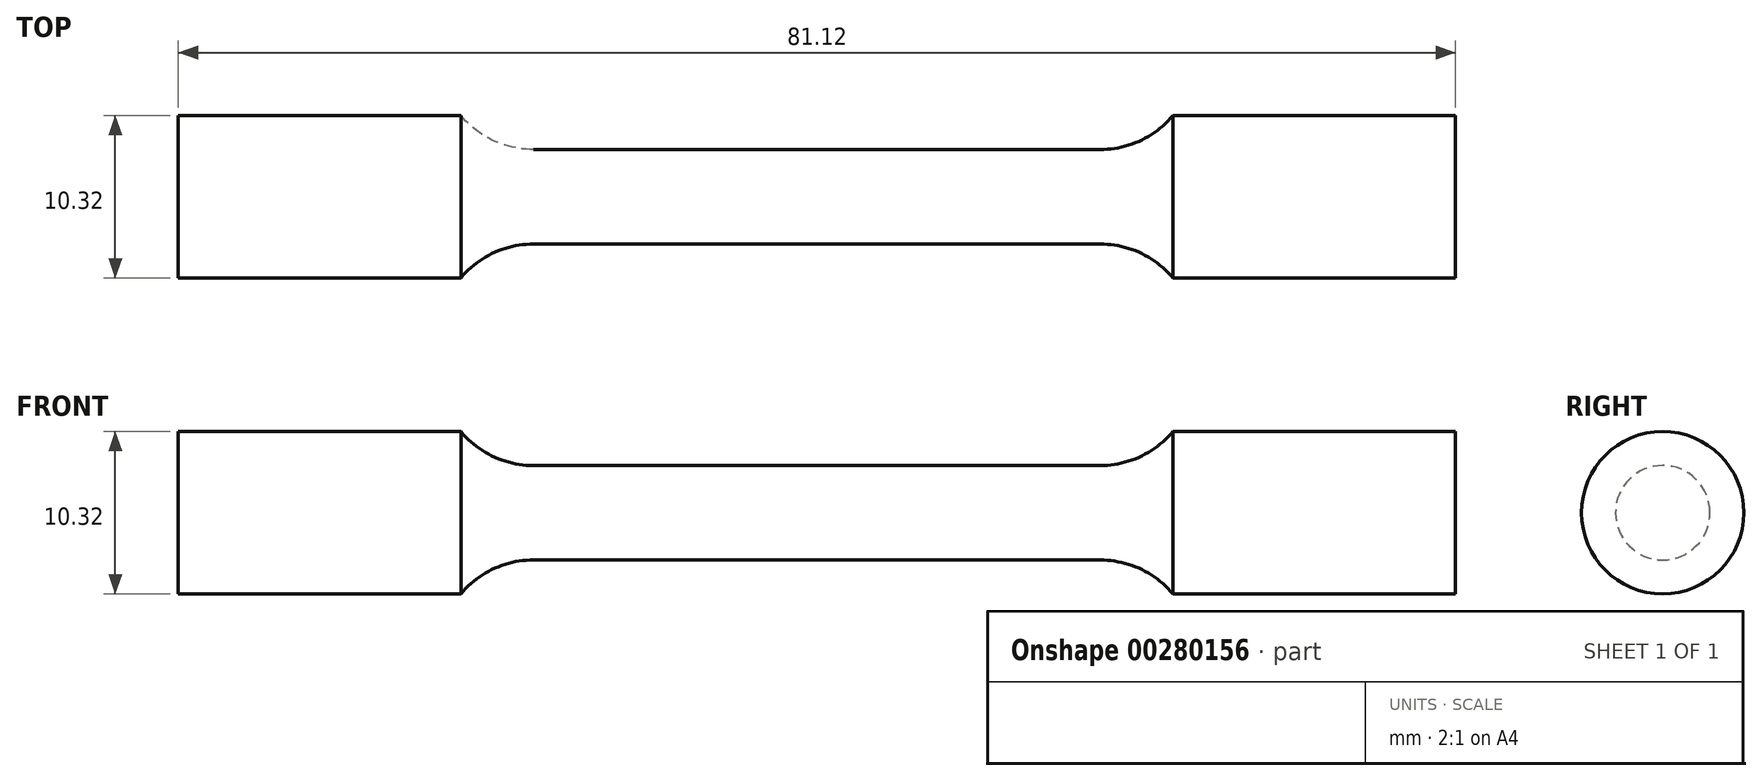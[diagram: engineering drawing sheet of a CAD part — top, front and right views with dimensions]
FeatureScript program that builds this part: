
annotation { "Feature Type Name" : "Feature", "Feature Type Description" : "" }
export const myFeature = defineFeature(function(context is Context, id is Id, definition is map)
    precondition{}
    {
        {
            var Q0;
            Q0=qCreatedBy(makeId("Front.planeOp"),FACE);
            var sketch = newSketch(context, id + "F0", { "sketchPlane" : qUnion([Q0])});
            skLineSegment(sketch, "E0", {"start": v(0, 3) * mm, "end": v(18, 3) * mm});
            skArc(sketch, "E1", {"start": v(18, 3) * mm, "mid": v(20.54, 3.57) * mm, "end": v(22.6, 5.16) * mm});
            skLineSegment(sketch, "E2", {"start": v(22.6, 5.16) * mm, "end": v(40.56, 5.16) * mm});
            skLineSegment(sketch, "E3", {"start": v(40.56, 5.16) * mm, "end": v(40.56, 0) * mm});
            skLineSegment(sketch, "E4.MirrorCS", {"start": v(0, 3) * mm, "end": v(-18, 3) * mm});
            skLineSegment(sketch, "E5.MirrorCS", {"start": v(-40.56, 5.16) * mm, "end": v(-40.56, 0) * mm});
            skLineSegment(sketch, "E6.MirrorCS", {"start": v(-22.6, 5.16) * mm, "end": v(-40.56, 5.16) * mm});
            skArc(sketch, "E7.MirrorCS", {"start": v(-18, 3) * mm, "mid": v(-20.54, 3.57) * mm, "end": v(-22.6, 5.16) * mm});
            skLineSegment(sketch, "E8", {"start": v(-40.56, 0) * mm, "end": v(40.56, 0) * mm});
            skSolve(sketch);
        }
        {
            var Q0;
            Q0 = qSketchRegion(id + "F0", true);
            var Q1;
            Q1=sQuery(id+"F0.wireOp",EDGE,"E8");
            revolve(context, id + "F1", {"entities" : qUnion([Q0]), "axis" : qUnion([Q1]), "revolveType" : RevolveType.FULL});
        }
    });
